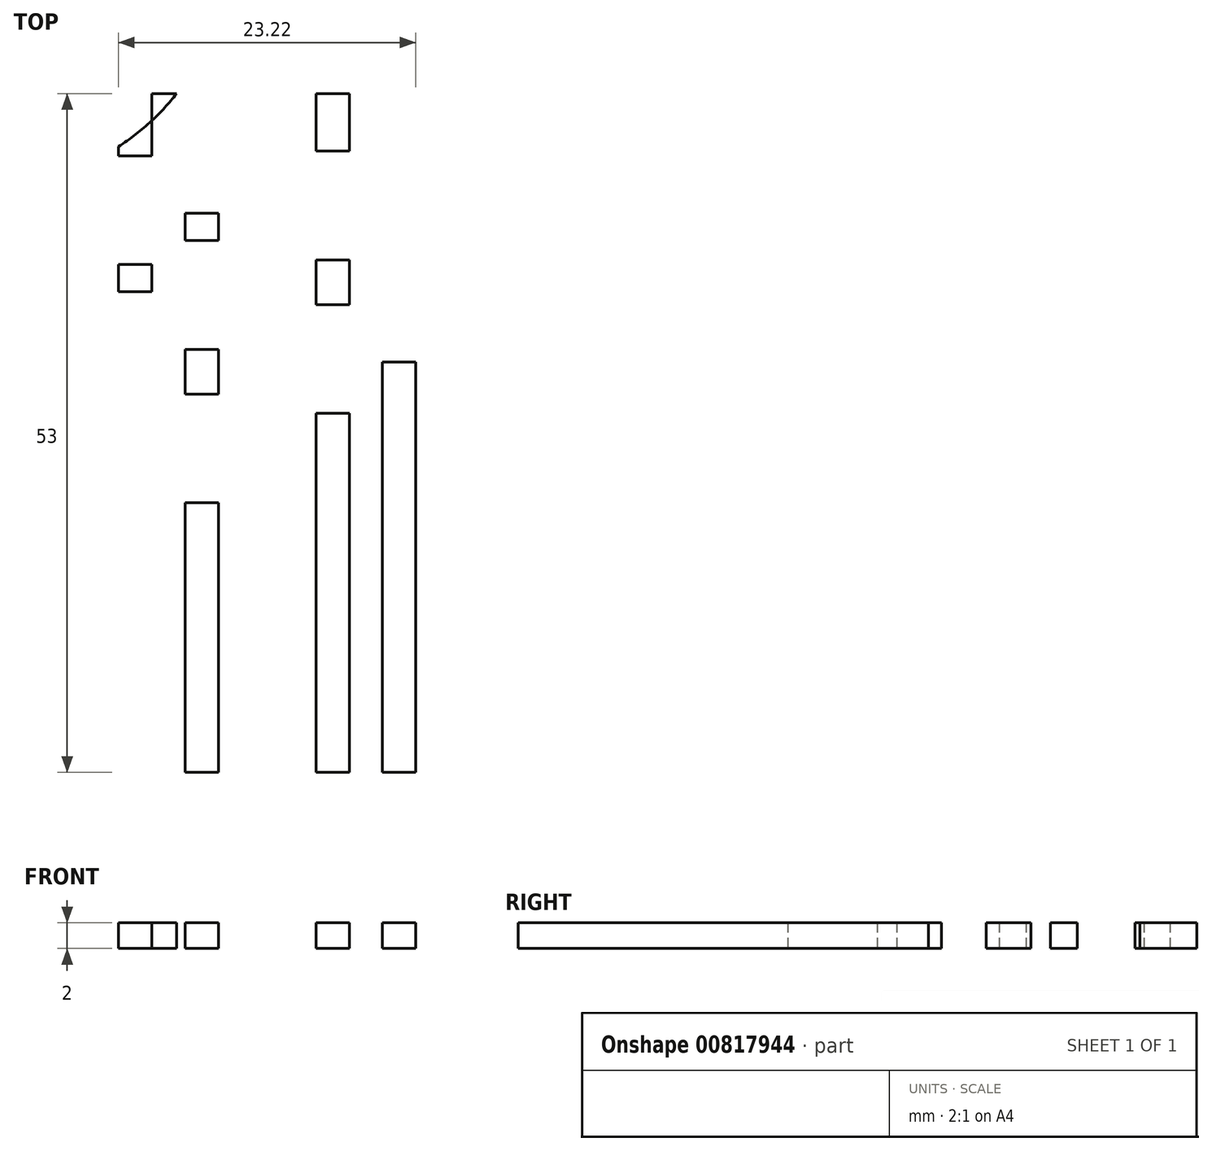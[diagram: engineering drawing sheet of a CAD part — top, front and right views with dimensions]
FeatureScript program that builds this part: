
annotation { "Feature Type Name" : "Feature", "Feature Type Description" : "" }
export const myFeature = defineFeature(function(context is Context, id is Id, definition is map)
    precondition{}
    {
        {
            var Q0;
            Q0=qCreatedBy(makeId("Top.planeOp"),FACE);
            var sketch = newSketch(context, id + "F0", { "sketchPlane" : qUnion([Q0])});
            skLineSegment(sketch, "E0.bottom", {"start": v(3.9, 26.5) * mm, "end": v(-3.9, 26.5) * mm});
            skLineSegment(sketch, "E0.top", {"start": v(3.9, -26.5) * mm, "end": v(-3.9, -26.5) * mm});
            skLineSegment(sketch, "E0.left", {"start": v(3.9, 26.5) * mm, "end": v(3.9, -26.5) * mm});
            skLineSegment(sketch, "E0.right", {"start": v(-3.9, 26.5) * mm, "end": v(-3.9, -26.5) * mm});
            skPoint(sketch, "E0.middle", {"position": v(0, 0) * mm});
            skCircle(sketch, "E1", {"center": v(-14.1, 38.1) * mm, "radius": 18.75 * mm});
            skLineSegment(sketch, "E2.bottom", {"start": v(-3.9, -26.5) * mm, "end": v(-1.3, -26.5) * mm});
            skLineSegment(sketch, "E2.top", {"start": v(-3.9, 26.5) * mm, "end": v(-1.3, 26.5) * mm});
            skLineSegment(sketch, "E2.left", {"start": v(-3.9, -26.5) * mm, "end": v(-3.9, 26.5) * mm});
            skLineSegment(sketch, "E2.right", {"start": v(-1.3, -26.5) * mm, "end": v(-1.3, 26.5) * mm});
            skLineSegment(sketch, "E3.bottom", {"start": v(-1.3, -26.5) * mm, "end": v(1.3, -26.5) * mm});
            skLineSegment(sketch, "E3.top", {"start": v(-1.3, 26.5) * mm, "end": v(1.3, 26.5) * mm});
            skLineSegment(sketch, "E3.right", {"start": v(1.3, -26.5) * mm, "end": v(1.3, 26.5) * mm});
            skLineSegment(sketch, "E4.bottom", {"start": v(1.3, 25.65) * mm, "end": v(3.9, 25.65) * mm});
            skLineSegment(sketch, "E4.top", {"start": v(1.3, 17.15) * mm, "end": v(3.9, 17.15) * mm});
            skLineSegment(sketch, "E4.left", {"start": v(1.3, 25.65) * mm, "end": v(1.3, 17.15) * mm});
            skLineSegment(sketch, "E4.right", {"start": v(3.9, 25.65) * mm, "end": v(3.9, 17.15) * mm});
            skLineSegment(sketch, "E5.bottom", {"start": v(-3.9, 21.65) * mm, "end": v(-1.3, 21.65) * mm});
            skLineSegment(sketch, "E5.top", {"start": v(-3.9, 13.15) * mm, "end": v(-1.3, 13.15) * mm});
            skLineSegment(sketch, "E5.left", {"start": v(-3.9, 21.65) * mm, "end": v(-3.9, 13.15) * mm});
            skLineSegment(sketch, "E5.right", {"start": v(-1.3, 21.65) * mm, "end": v(-1.3, 13.15) * mm});
            skLineSegment(sketch, "E6.bottom", {"start": v(1.3, 15.05) * mm, "end": v(3.9, 15.05) * mm});
            skLineSegment(sketch, "E6.top", {"start": v(1.3, 6.55) * mm, "end": v(3.9, 6.55) * mm});
            skLineSegment(sketch, "E6.left", {"start": v(1.3, 15.05) * mm, "end": v(1.3, 6.55) * mm});
            skLineSegment(sketch, "E6.right", {"start": v(3.9, 15.05) * mm, "end": v(3.9, 6.55) * mm});
            skLineSegment(sketch, "E7.bottom", {"start": v(-3.9, 11.04) * mm, "end": v(-1.3, 11.04) * mm});
            skLineSegment(sketch, "E7.top", {"start": v(-3.9, 2.54) * mm, "end": v(-1.3, 2.54) * mm});
            skLineSegment(sketch, "E7.left", {"start": v(-3.9, 11.04) * mm, "end": v(-3.9, 2.54) * mm});
            skLineSegment(sketch, "E7.right", {"start": v(-1.3, 11.04) * mm, "end": v(-1.3, 2.54) * mm});
            skLineSegment(sketch, "E8.bottom", {"start": v(-1.3, -1.46) * mm, "end": v(1.3, -1.46) * mm});
            skLineSegment(sketch, "E8.top", {"start": v(-1.3, 7.04) * mm, "end": v(1.3, 7.04) * mm});
            skLineSegment(sketch, "E8.left", {"start": v(-1.3, -1.46) * mm, "end": v(-1.3, 7.04) * mm});
            skLineSegment(sketch, "E8.right", {"start": v(1.3, -1.46) * mm, "end": v(1.3, 7.04) * mm});
            skLineSegment(sketch, "E9.bottom", {"start": v(1.3, -5.46) * mm, "end": v(3.9, -5.46) * mm});
            skLineSegment(sketch, "E9.top", {"start": v(1.3, 3.04) * mm, "end": v(3.9, 3.04) * mm});
            skLineSegment(sketch, "E9.left", {"start": v(1.3, -5.46) * mm, "end": v(1.3, 3.04) * mm});
            skLineSegment(sketch, "E9.right", {"start": v(3.9, -5.46) * mm, "end": v(3.9, 3.04) * mm});
            skLineSegment(sketch, "E10.bottom", {"start": v(11.52, -26.5) * mm, "end": v(19.32, -26.5) * mm});
            skLineSegment(sketch, "E10.top", {"start": v(11.52, 26.5) * mm, "end": v(19.32, 26.5) * mm});
            skLineSegment(sketch, "E10.left", {"start": v(11.52, -26.5) * mm, "end": v(11.52, 26.5) * mm});
            skLineSegment(sketch, "E10.right", {"start": v(19.32, -26.5) * mm, "end": v(19.32, 26.5) * mm});
            skLineSegment(sketch, "E11.bottom", {"start": v(11.52, -26.5) * mm, "end": v(14.12, -26.5) * mm});
            skLineSegment(sketch, "E11.top", {"start": v(11.52, 26.5) * mm, "end": v(14.12, 26.5) * mm});
            skLineSegment(sketch, "E11.right", {"start": v(14.12, -26.5) * mm, "end": v(14.12, 26.5) * mm});
            skLineSegment(sketch, "E12.bottom", {"start": v(14.12, -26.5) * mm, "end": v(16.72, -26.5) * mm});
            skLineSegment(sketch, "E12.top", {"start": v(14.12, 26.5) * mm, "end": v(16.72, 26.5) * mm});
            skLineSegment(sketch, "E12.right", {"start": v(16.72, -26.5) * mm, "end": v(16.72, 26.5) * mm});
            skLineSegment(sketch, "E13.bottom", {"start": v(11.52, 13.53) * mm, "end": v(14.12, 13.53) * mm});
            skLineSegment(sketch, "E13.top", {"start": v(11.52, 22.03) * mm, "end": v(14.12, 22.03) * mm});
            skLineSegment(sketch, "E13.left", {"start": v(11.52, 13.53) * mm, "end": v(11.52, 22.03) * mm});
            skLineSegment(sketch, "E13.right", {"start": v(14.12, 13.53) * mm, "end": v(14.12, 22.03) * mm});
            skLineSegment(sketch, "E14.bottom", {"start": v(14.12, 18.03) * mm, "end": v(16.72, 18.03) * mm});
            skLineSegment(sketch, "E14.top", {"start": v(14.12, 9.53) * mm, "end": v(16.72, 9.53) * mm});
            skLineSegment(sketch, "E14.left", {"start": v(14.12, 18.03) * mm, "end": v(14.12, 9.53) * mm});
            skLineSegment(sketch, "E14.right", {"start": v(16.72, 18.03) * mm, "end": v(16.72, 9.53) * mm});
            skLineSegment(sketch, "E15.bottom", {"start": v(16.72, 14.03) * mm, "end": v(19.32, 14.03) * mm});
            skLineSegment(sketch, "E15.top", {"start": v(16.72, 5.53) * mm, "end": v(19.32, 5.53) * mm});
            skLineSegment(sketch, "E15.left", {"start": v(16.72, 14.03) * mm, "end": v(16.72, 5.53) * mm});
            skLineSegment(sketch, "E15.right", {"start": v(19.32, 14.03) * mm, "end": v(19.32, 5.53) * mm});
            skLineSegment(sketch, "E16.bottom", {"start": v(11.52, 10.03) * mm, "end": v(14.12, 10.03) * mm});
            skLineSegment(sketch, "E16.top", {"start": v(11.52, 1.53) * mm, "end": v(14.12, 1.53) * mm});
            skLineSegment(sketch, "E16.left", {"start": v(11.52, 10.03) * mm, "end": v(11.52, 1.53) * mm});
            skLineSegment(sketch, "E16.right", {"start": v(14.12, 10.03) * mm, "end": v(14.12, 1.53) * mm});
            skSolve(sketch);
        }
        {
            var Q0;
            {var subQ5=sQuery(id+"F0.wireOp",EDGE,"E5.bottom");Q0=makeQuery(id+"F0.imprint","IMPRINT",FACE,{"disambiguationData":[TD([[makeQuery(id+"F0.imprint","IMPRINT",EDGE,{"derivedFrom":subQ5}),1.0]])]});}
            var Q1;
            {var subQ0=sQuery(id+"F0.wireOp",EDGE,"E0.bottom");Q1=makeQuery(id+"F0.imprint","IMPRINT",FACE,{"disambiguationData":[TD([[makeQuery(id+"F0.imprint","IMPRINT",EDGE,{"derivedFrom":subQ0}),1.0]])]});}
            var Q2;
            {var subQ1=sQuery(id+"F0.wireOp",EDGE,"E4.left");Q2=makeQuery(id+"F0.imprint","IMPRINT",FACE,{"disambiguationData":[TD([[makeQuery(id+"F0.imprint","IMPRINT",EDGE,{"derivedFrom":subQ1}),-1.0]])]});}
            var Q3;
            {var subQ0=sQuery(id+"F0.wireOp",EDGE,"E4.top");Q3=makeQuery(id+"F0.imprint","IMPRINT",FACE,{"disambiguationData":[TD([[makeQuery(id+"F0.imprint","IMPRINT",EDGE,{"derivedFrom":subQ0}),-1.0]])]});}
            var Q4;
            {var subQ0=sQuery(id+"F0.wireOp",EDGE,"E5.top");Q4=makeQuery(id+"F0.imprint","IMPRINT",FACE,{"disambiguationData":[TD([[makeQuery(id+"F0.imprint","IMPRINT",EDGE,{"derivedFrom":subQ0}),-1.0]])]});}
            var Q5;
            {var subQ0=sQuery(id+"F0.wireOp",EDGE,"E6.top");Q5=makeQuery(id+"F0.imprint","IMPRINT",FACE,{"disambiguationData":[TD([[makeQuery(id+"F0.imprint","IMPRINT",EDGE,{"derivedFrom":subQ0}),-1.0]])]});}
            var Q6;
            {var subQ2=sQuery(id+"F0.wireOp",EDGE,"E2.bottom");Q6=makeQuery(id+"F0.imprint","IMPRINT",FACE,{"disambiguationData":[TD([[makeQuery(id+"F0.imprint","IMPRINT",EDGE,{"derivedFrom":subQ2}),1.0]])]});}
            var Q7;
            {var subQ2=sQuery(id+"F0.wireOp",EDGE,"E3.bottom");Q7=makeQuery(id+"F0.imprint","IMPRINT",FACE,{"disambiguationData":[TD([[makeQuery(id+"F0.imprint","IMPRINT",EDGE,{"derivedFrom":subQ2}),1.0]])]});}
            var Q8;
            {var subQ0=sQuery(id+"F0.wireOp",EDGE,"E0.top");Q8=makeQuery(id+"F0.imprint","IMPRINT",FACE,{"disambiguationData":[TD([[makeQuery(id+"F0.imprint","IMPRINT",EDGE,{"derivedFrom":subQ0}),-1.0]])]});}
            var Q9;
            {var subQ0=sQuery(id+"F0.wireOp",EDGE,"E11.top");Q9=makeQuery(id+"F0.imprint","IMPRINT",FACE,{"disambiguationData":[TD([[makeQuery(id+"F0.imprint","IMPRINT",EDGE,{"derivedFrom":subQ0}),-1.0]])]});}
            var Q10;
            {var subQ2=sQuery(id+"F0.wireOp",EDGE,"E12.top");Q10=makeQuery(id+"F0.imprint","IMPRINT",FACE,{"disambiguationData":[TD([[makeQuery(id+"F0.imprint","IMPRINT",EDGE,{"derivedFrom":subQ2}),-1.0]])]});}
            var Q11;
            {var subQ1=sQuery(id+"F0.wireOp",EDGE,"E10.top");Q11=makeQuery(id+"F0.imprint","IMPRINT",FACE,{"disambiguationData":[TD([[makeQuery(id+"F0.imprint","IMPRINT",EDGE,{"derivedFrom":subQ1}),-1.0]])]});}
            var Q12;
            {var subQ0=sQuery(id+"F0.wireOp",EDGE,"E13.bottom");Q12=makeQuery(id+"F0.imprint","IMPRINT",FACE,{"disambiguationData":[TD([[makeQuery(id+"F0.imprint","IMPRINT",EDGE,{"derivedFrom":subQ0}),-1.0]])]});}
            var Q13;
            {var subQ1=sQuery(id+"F0.wireOp",EDGE,"E12.bottom");Q13=makeQuery(id+"F0.imprint","IMPRINT",FACE,{"disambiguationData":[TD([[makeQuery(id+"F0.imprint","IMPRINT",EDGE,{"derivedFrom":subQ1}),1.0]])]});}
            var Q14;
            {var subQ0=sQuery(id+"F0.wireOp",EDGE,"E10.bottom");Q14=makeQuery(id+"F0.imprint","IMPRINT",FACE,{"disambiguationData":[TD([[makeQuery(id+"F0.imprint","IMPRINT",EDGE,{"derivedFrom":subQ0}),1.0]])]});}
            var Q15;
            {var subQ0=sQuery(id+"F0.wireOp",EDGE,"E11.bottom");Q15=makeQuery(id+"F0.imprint","IMPRINT",FACE,{"disambiguationData":[TD([[makeQuery(id+"F0.imprint","IMPRINT",EDGE,{"derivedFrom":subQ0}),1.0]])]});}
            extrude(context, id + "F1", {"entities" : qUnion([Q0, Q1, Q2, Q3, Q4, Q5, Q6, Q7, Q8, Q9, Q10, Q11, Q12, Q13, Q14, Q15]), "depth" : 2 * mm, "offsetDistance" : 25 * mm});
        }
    });
